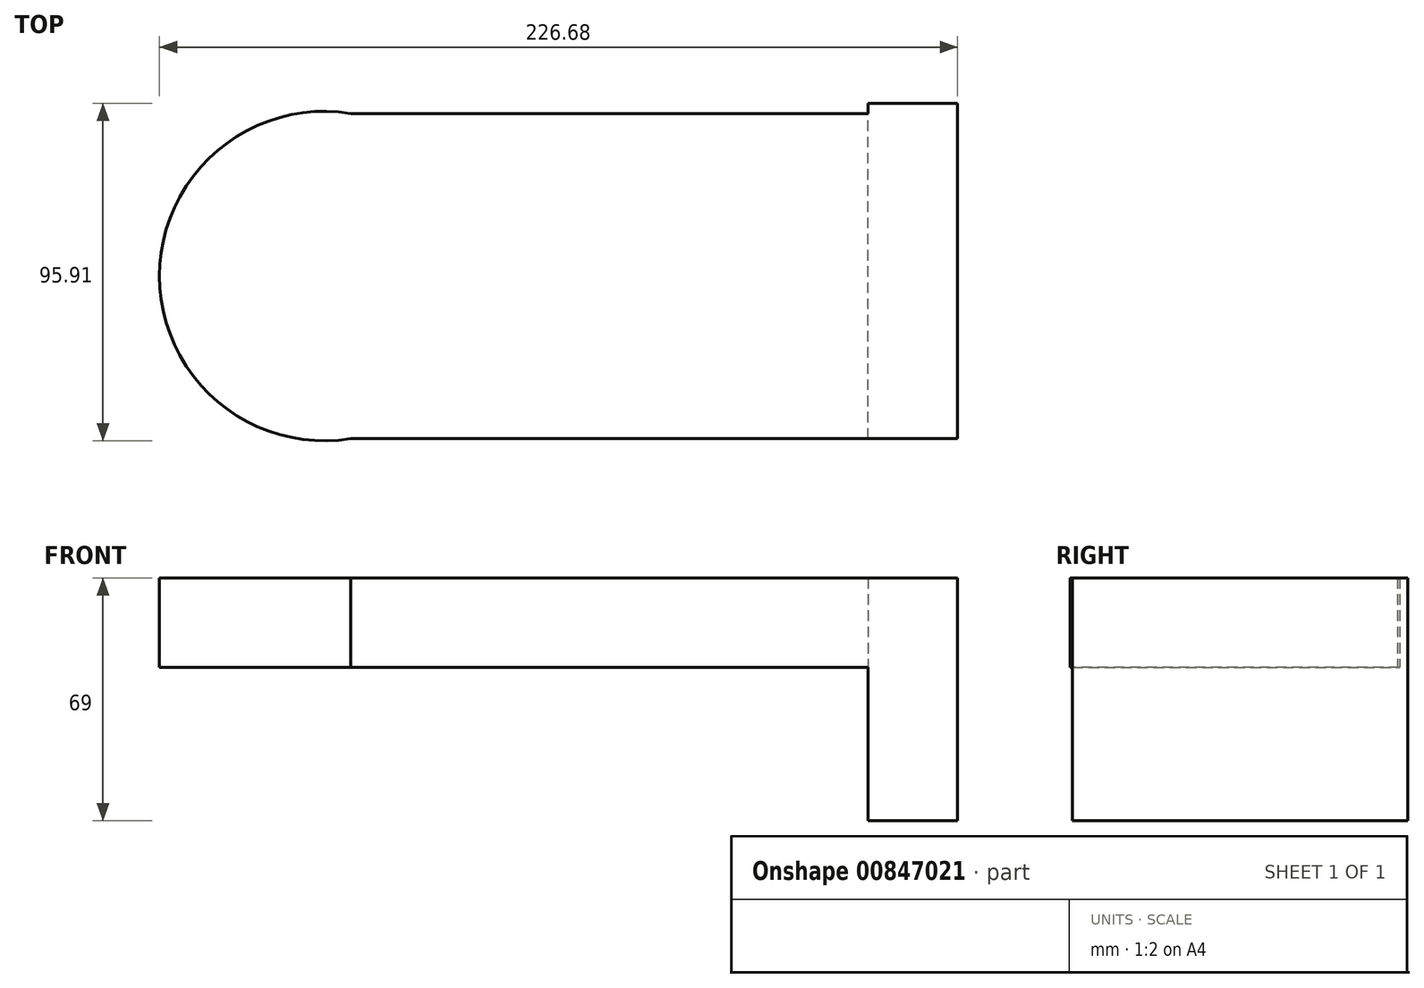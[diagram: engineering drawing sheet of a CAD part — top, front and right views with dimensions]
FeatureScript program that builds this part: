
annotation { "Feature Type Name" : "Feature", "Feature Type Description" : "" }
export const myFeature = defineFeature(function(context is Context, id is Id, definition is map)
    precondition{}
    {
        {
            var Q0;
            Q0=qCreatedBy(makeId("Top.planeOp"),FACE);
            var sketch = newSketch(context, id + "F0", { "sketchPlane" : qUnion([Q0])});
            skLineSegment(sketch, "E0.bottom", {"start": v(77.24, -46.2) * mm, "end": v(-77.24, -46.2) * mm});
            skLineSegment(sketch, "E0.top", {"start": v(77.24, 46.2) * mm, "end": v(-77.24, 46.2) * mm});
            skLineSegment(sketch, "E0.left", {"start": v(77.24, -46.2) * mm, "end": v(77.24, 46.2) * mm});
            skLineSegment(sketch, "E0.right", {"start": v(-77.24, -46.2) * mm, "end": v(-77.24, 46.2) * mm});
            skPoint(sketch, "E0.middle", {"position": v(0, 0) * mm});
            skCircle(sketch, "E1", {"center": v(-77.24, 0) * mm, "radius": 46.8 * mm});
            skSolve(sketch);
        }
        {
            var Q0;
            {var subQ0=sQuery(id+"F0.wireOp",EDGE,"E0.right");Q0=makeQuery(id+"F0.imprint","IMPRINT",FACE,{"disambiguationData":[TD([[makeQuery(id+"F0.imprint","IMPRINT",EDGE,{"derivedFrom":subQ0}),-1.0]])]});}
            var Q1;
            {var subQ0=sQuery(id+"F0.wireOp",EDGE,"E0.left");Q1=makeQuery(id+"F0.imprint","IMPRINT",FACE,{"disambiguationData":[TD([[makeQuery(id+"F0.imprint","IMPRINT",EDGE,{"derivedFrom":subQ0}),1.0]])]});}
            var Q2;
            {var subQ0=sQuery(id+"F0.wireOp",EDGE,"E0.right");Q2=makeQuery(id+"F0.imprint","IMPRINT",FACE,{"disambiguationData":[TD([[makeQuery(id+"F0.imprint","IMPRINT",EDGE,{"derivedFrom":subQ0}),1.0]])]});}
            var Q3;
            Q3 = qSketchRegion(id + "F0", true);
            extrude(context, id + "F1", {"entities" : qUnion([Q0, Q1, Q2, Q3]), "depth" : 25.4 * mm, "offsetDistance" : 25.4 * mm});
        }
        {
            var Q0;
            Q0=makeQuery(id+"F1.opExtrude","SWEPT_FACE",FACE,{"disambiguationData":[OSD([sQuery(id+"F0.wireOp",EDGE,"E0.left")])]});
            var sketch = newSketch(context, id + "F2", { "sketchPlane" : qUnion([Q0])});
            skLineSegment(sketch, "E2.bottom", {"start": v(-46.2, 25.4) * mm, "end": v(49.1, 25.4) * mm});
            skLineSegment(sketch, "E2.top", {"start": v(-46.2, -43.6) * mm, "end": v(49.1, -43.6) * mm});
            skLineSegment(sketch, "E2.left", {"start": v(-46.2, 25.4) * mm, "end": v(-46.2, -43.6) * mm});
            skLineSegment(sketch, "E2.right", {"start": v(49.1, 25.4) * mm, "end": v(49.1, -43.6) * mm});
            skSolve(sketch);
        }
        {
            var Q0;
            {var subQ4=sQuery(id+"F2.wireOp",EDGE,"E2.top");Q0=makeQuery(id+"F2.imprint","IMPRINT",FACE,{"disambiguationData":[TD([[makeQuery(id+"F2.imprint","IMPRINT",EDGE,{"derivedFrom":subQ4}),1.0]])]});}
            var Q1;
            {var subQ3=sQuery(id+"F0.wireOp",EDGE,"E0.left");var subQ5=makeQuery(id+"F1.opExtrude","CAP_EDGE",EDGE,{"disambiguationData":[OSD([subQ3])],"isStart":true});Q1=makeQuery(id+"F2.imprint","IMPRINT",FACE,{"disambiguationData":[TD([[makeQuery(id+"F2.imprint","IMPRINT",EDGE,{"derivedFrom":subQ5}),1.0]])]});}
            extrude(context, id + "F3", {"entities" : qUnion([Q0, Q1]), "operationType" : NewBodyOperationType.ADD, "depth" : 25.4 * mm, "offsetDistance" : 25.4 * mm});
        }
    });
